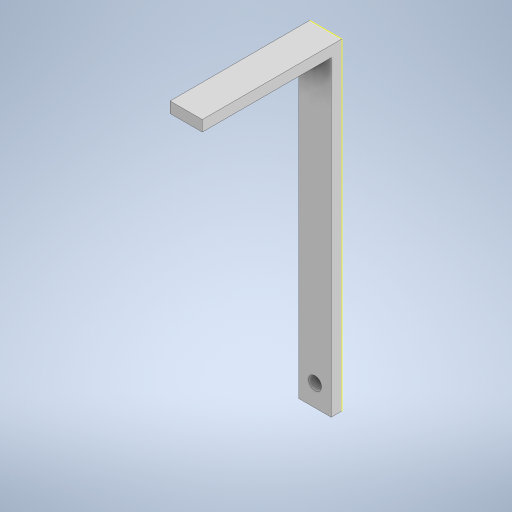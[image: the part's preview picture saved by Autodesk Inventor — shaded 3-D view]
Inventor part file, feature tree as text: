
AUTODESK INVENTOR PART (.ipt)
format: ipt  version: 2023 (Build 270158000, 158)  size: 250,368 bytes
history: native  units: in
note: dims shown in document units (in); Inventor stores cm internally (conversion verified against a paired STEP export)
features: sketch x5, extrude x2, hole x1, projected_geometry x1
ambient origin geometry x8: Origin, YZ Plane, XZ Plane, XY Plane, X Axis, Y Axis, Z Axis, Center Point
bodies: Solid1 (feature_tree)
feature tree (9):
  sketch  "Sketch1"  dims[d0=0.5906in d1=0.1969in]
  extrude  "Extrusion1"  Depth=0.1969in
  extrude  "Extrusion2"  Depth=2.3622in TaperAngle=0.0deg
  sketch  "Sketch4"  dims[d7=0.2362in d8=0.2362in d9=0.1575in d10=0.0787in d11=90.0deg d12=0.315in d13=0.8108in]
  hole  "Hole1"  [1 undecoded]
  sketch  "Sketch2"  dims[d2=5.9055in d3=0.0in d4=2.3622in d5=0.0in]
  sketch  "Sketch3"  dims[d6=0.2362in]
  projected_geometry  "Projected Loop1"
  sketch  "Sketch5"
note: 1 required parameter value undecoded (feature->parameter linkage not recoverable at this tier; creation-order binding heuristic only, values carry confidence <= 0.55)
